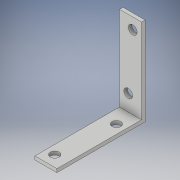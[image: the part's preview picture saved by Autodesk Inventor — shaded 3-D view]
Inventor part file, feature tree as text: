
AUTODESK INVENTOR PART (.ipt)
format: ipt  version: 2018 (Build 220112000, 112)  size: 122,368 bytes
history: native  units: in
note: dims shown in document units (in); Inventor stores cm internally (conversion verified against a paired STEP export)
features: extrude x5, sketch x3
ambient origin geometry x8: Origin, YZ Plane, XZ Plane, XY Plane, X Axis, Y Axis, Z Axis, Center Point
bodies: Solid1 (feature_tree)
feature tree (8):
  extrude  "Extrusion1"  Depth=2.5in
  sketch  "Sketch2"  dims[d2=0.1in d3=0.1in]
  extrude  "Extrusion2"  Depth=0.1in
  extrude  "Extrusion3"  Depth=0.625in
  sketch  "Sketch3"  dims[d4=0.625in d5=0.0in d6=0.25in d7=0.25in d8=0.625in d9=0.0in d10=0.625in d11=0.0in d12=0.25in d13=0.25in d14=0.25in d15=0.3125in d16=1.625in d17=0.375in d18=0.625in d19=0.0in d20=0.625in d21=0.0in]
  extrude  "Extrusion4"  Depth=0.625in
  extrude  "Extrusion5"  Depth=0.625in TaperAngle=0.0deg
  sketch  "Sketch1"  dims[d0=2.5in d1=2.5in]
